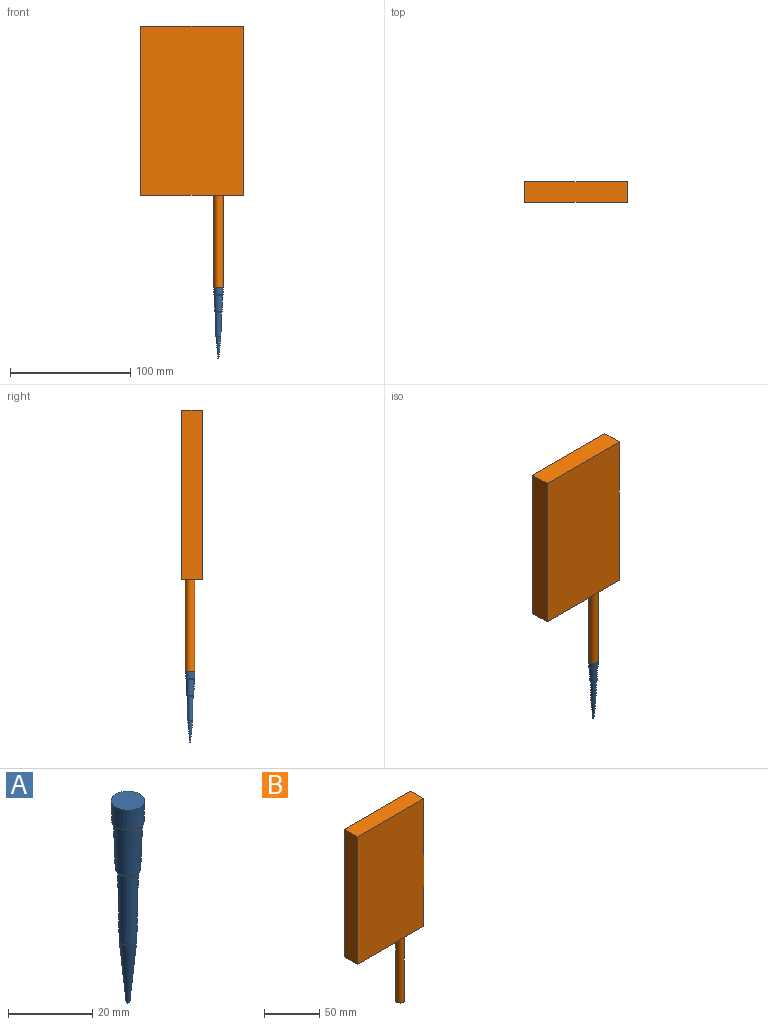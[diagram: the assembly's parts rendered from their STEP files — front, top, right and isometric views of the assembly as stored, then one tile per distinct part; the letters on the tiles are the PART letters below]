
ASSEMBLY  parts=2 mates=1
PART A: 8 faces, bbox 7.9x7.9x58.5 mm
  f0: plane 0.9x0.9mm, normal (0,0,-1), area 0.6mm2, adj f1
  f1: cone r=2.1mm half-angle=5.3deg, axis (0,0,1), area 144mm2, adj f0,f2
  f2: cone r=2.46mm half-angle=1deg, axis (0,0,1), area 287.9mm2, adj f1,f3
  f3: cone r=2.46mm half-angle=37.2deg, axis (0,0,1), area 16.3mm2, adj f2,f4
  f4: cone r=3.49mm half-angle=1.9deg, axis (0,0,1), area 280.6mm2, adj f3,f5
  f5: cone r=3.49mm half-angle=54.2deg, axis (0,0,1), area 11.9mm2, adj f4,f6
  f6: cone r=3.95mm half-angle=0.5deg, axis (0,0,1), area 142.7mm2, adj f5,f7
  f7: plane 7.9x7.9mm, normal (0,0,1), area 49mm2, adj f6
PART B: 8 faces, bbox 85x17x218.1 mm
  f0: plane 85x17mm, normal (0,0,1), area 1445mm2, adj f1,f3,f4,f5
  f1: plane 141.1x17mm, normal (-1,0,0), area 2398.7mm2, adj f0,f2,f4,f5
  f2: plane 85x17mm, normal (0,0,-1), area 1394.7mm2, adj f1,f3,f4,f5,f6
  f3: plane 141.1x17mm, normal (1,0,0), area 2398.7mm2, adj f0,f2,f4,f5
  f4: plane 141.1x85mm, normal (0,-1,0), area 11993.5mm2, adj f0,f1,f2,f3
  f5: plane 141.1x85mm, normal (0,1,0), area 11993.5mm2, adj f0,f1,f2,f3
  f6: cylinder r=4mm len=77mm, axis (0,0,1), area 1935.2mm2, adj f2,f7
  f7: plane 8x8mm, normal (0,0,-1), area 50.3mm2, adj f6
PLACE A t=(0.82,-6.15,-130.42)mm
PLACE B t=(-63.68,0.85,-25.19)mm
MATE fastened A.f1 <-> B.f6  axis (0,0,1) through (0.82,-6.15,-102.19)mm
